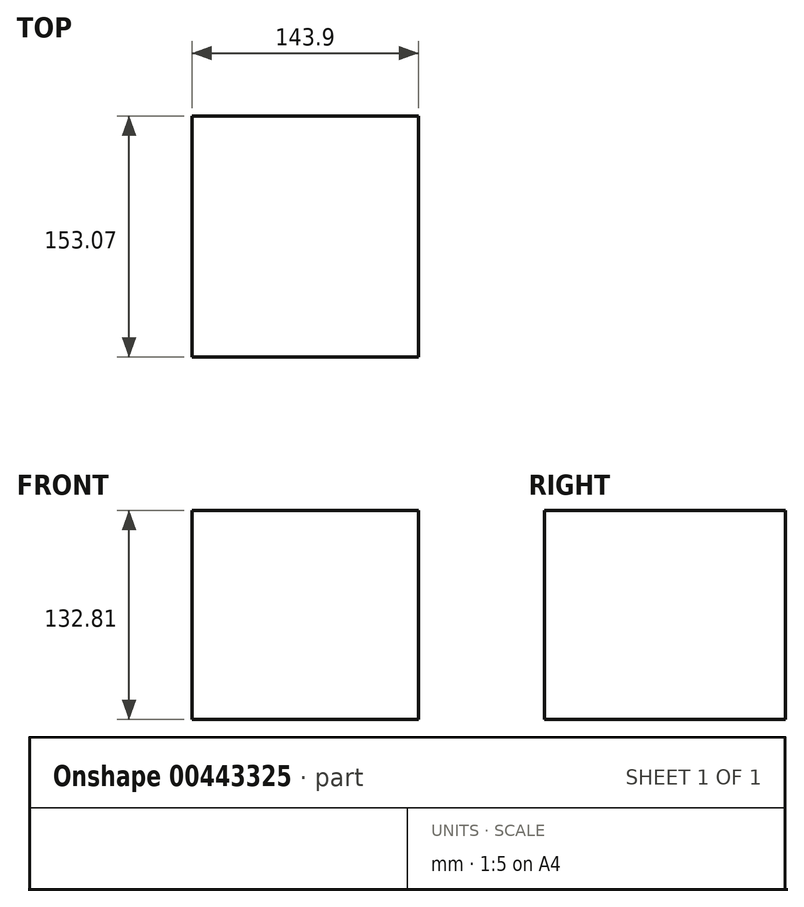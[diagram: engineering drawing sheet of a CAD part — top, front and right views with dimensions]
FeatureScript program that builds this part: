
annotation { "Feature Type Name" : "Feature", "Feature Type Description" : "" }
export const myFeature = defineFeature(function(context is Context, id is Id, definition is map)
    precondition{}
    {
        {
            var Q0;
            Q0=qCreatedBy(makeId("Top.planeOp"),FACE);
            var sketch = newSketch(context, id + "F0", { "sketchPlane" : qUnion([Q0])});
            skLineSegment(sketch, "E0.bottom", {"start": v(71.02, 77.51) * mm, "end": v(-72.88, 77.51) * mm});
            skLineSegment(sketch, "E0.top", {"start": v(71.02, -75.56) * mm, "end": v(-72.88, -75.56) * mm});
            skLineSegment(sketch, "E0.left", {"start": v(71.02, 77.51) * mm, "end": v(71.02, -75.56) * mm});
            skLineSegment(sketch, "E0.right", {"start": v(-72.88, 77.51) * mm, "end": v(-72.88, -75.56) * mm});
            skSolve(sketch);
        }
        {
            var Q0;
            Q0 = qSketchRegion(id + "F0", true);
            extrude(context, id + "F1", {"entities" : qUnion([Q0]), "depth" : 132.8 * mm});
        }
    });
